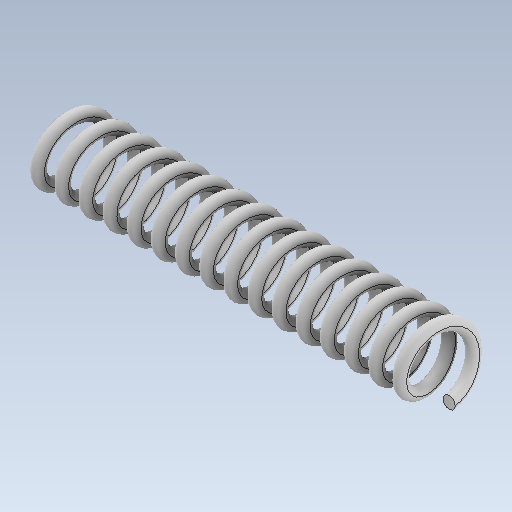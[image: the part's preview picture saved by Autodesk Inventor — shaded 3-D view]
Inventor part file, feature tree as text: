
AUTODESK INVENTOR PART (.ipt)
format: ipt  version: 2021 (Build 250183000, 183)  size: 392,704 bytes
history: native  units: mm
features: helix x1, sketch x1
ambient origin geometry x8: Origin, YZ Plane, XZ Plane, XY Plane, X Axis, Y Axis, Z Axis, Center Point
bodies: Solid1 (feature_tree)
feature tree (2):
  helix  "Coil1"  [1 undecoded]
  sketch  "Sketch1"  dims[d1=6.0mm d2=6.0mm d3=15.0mm d4=15.0mm d5=198.0mm d6=12.0mm d7=12.0mm d8=10.0mm d9=160.0mm d10=0.0mm d11=90.0deg d12=90.0deg d13=0.0mm d14=0.0mm]
note: 1 required parameter value undecoded (feature->parameter linkage not recoverable at this tier; creation-order binding heuristic only, values carry confidence <= 0.55)
